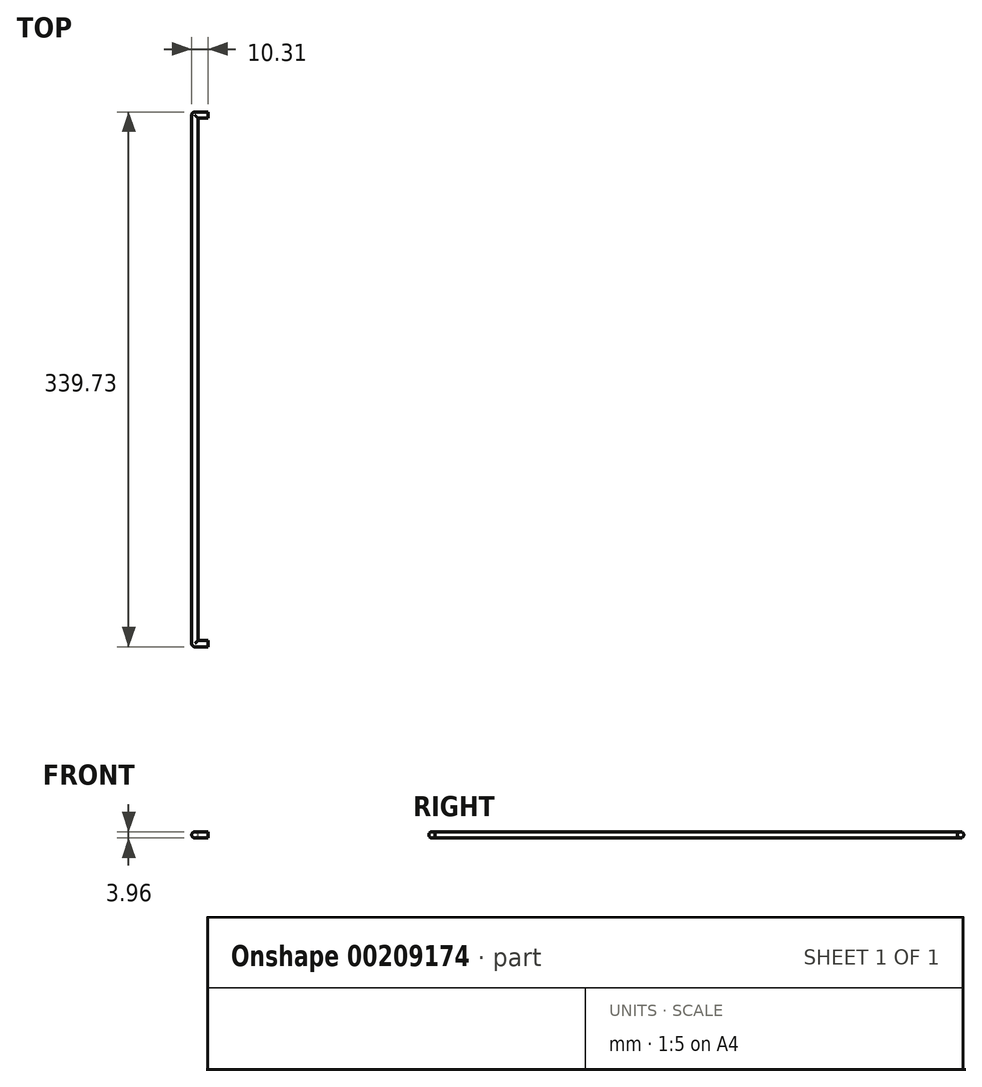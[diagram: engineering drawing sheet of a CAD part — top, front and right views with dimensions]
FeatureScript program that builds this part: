
annotation { "Feature Type Name" : "Feature", "Feature Type Description" : "" }
export const myFeature = defineFeature(function(context is Context, id is Id, definition is map)
    precondition{}
    {
        {
            var Q0;
            Q0=qCreatedBy(makeId("Front.planeOp"),FACE);
            var sketch = newSketch(context, id + "F0", { "sketchPlane" : qUnion([Q0])});
            skLineSegment(sketch, "E0.bottom", {"start": v(1.98, -1.98) * mm, "end": v(-1.98, -1.98) * mm});
            skLineSegment(sketch, "E0.top", {"start": v(1.98, 1.98) * mm, "end": v(-1.98, 1.98) * mm});
            skLineSegment(sketch, "E0.left", {"start": v(1.98, -1.98) * mm, "end": v(1.98, 1.98) * mm});
            skLineSegment(sketch, "E0.right", {"start": v(-1.98, -1.98) * mm, "end": v(-1.98, 1.98) * mm});
            skPoint(sketch, "E0.middle", {"position": v(0, 0) * mm});
            skSolve(sketch);
        }
        {
            var Q0;
            Q0 = qSketchRegion(id + "F0", true);
            extrude(context, id + "F1", {"entities" : qUnion([Q0]), "depth" : 339.72 * mm});
        }
        {
            var Q0;
            Q0=makeQuery(id+"F1.opExtrude","SWEPT_FACE",FACE,{"disambiguationData":[OSD([sQuery(id+"F0.wireOp",EDGE,"E0.left")])]});
            var sketch = newSketch(context, id + "F2", { "sketchPlane" : qUnion([Q0])});
            skLineSegment(sketch, "E1.bottom", {"start": v(-335.76, 1.98) * mm, "end": v(-339.73, 1.98) * mm});
            skLineSegment(sketch, "E1.top", {"start": v(-335.76, -1.98) * mm, "end": v(-339.73, -1.98) * mm});
            skLineSegment(sketch, "E1.left", {"start": v(-335.76, 1.98) * mm, "end": v(-335.76, -1.98) * mm});
            skLineSegment(sketch, "E1.right", {"start": v(-339.73, 1.98) * mm, "end": v(-339.73, -1.98) * mm});
            skPoint(sketch, "E1.middle", {"position": v(-337.74, 0) * mm});
            skLineSegment(sketch, "E2.left", {"start": v(-339.73, 0) * mm, "end": v(-339.73, 0) * mm});
            skLineSegment(sketch, "E2.right", {"start": v(-335.76, 0) * mm, "end": v(-335.76, 0) * mm});
            skLineSegment(sketch, "E3.bottom", {"start": v(0, 1.98) * mm, "end": v(-3.96, 1.98) * mm});
            skLineSegment(sketch, "E3.top", {"start": v(0, -1.98) * mm, "end": v(-3.96, -1.98) * mm});
            skLineSegment(sketch, "E3.left", {"start": v(0, 1.98) * mm, "end": v(0, -1.98) * mm});
            skLineSegment(sketch, "E3.right", {"start": v(-3.96, 1.98) * mm, "end": v(-3.96, -1.98) * mm});
            skPoint(sketch, "E3.middle", {"position": v(-1.98, 0) * mm});
            skSolve(sketch);
        }
        {
            var Q0;
            Q0 = qSketchRegion(id + "F2", true);
            extrude(context, id + "F3", {"entities" : qUnion([Q0]), "operationType" : NewBodyOperationType.ADD, "depth" : 6.35 * mm});
        }
        {
            var Q0;
            Q0=makeQuery(id+"F3.boolean.opBoolean","MERGE",EDGE,{"derivedFrom":[makeQuery(id+"F1.opExtrude","CAP_EDGE",EDGE,{"disambiguationData":[OSD([sQuery(id+"F0.wireOp",EDGE,"E0.top")])],"isStart":true}),makeQuery(id+"F3.opExtrude","SWEPT_EDGE",EDGE,{"disambiguationData":[OSD([sQuery(id+"F2.wireOp",EDGE,"E3.bottom"),sQuery(id+"F2.wireOp",EDGE,"E3.left")])]})]});
            var Q1;
            Q1=makeQuery(id+"F3.opExtrude","SWEPT_EDGE",EDGE,{"disambiguationData":[OSD([sQuery(id+"F0.wireOp",EDGE,"E0.top"),sQuery(id+"F0.wireOp",EDGE,"E0.left"),sQuery(id+"F2.wireOp",EDGE,"E3.bottom"),sQuery(id+"F2.wireOp",EDGE,"E3.right")])]});
            var Q2;
            Q2=makeQuery(id+"F3.boolean.opBoolean","MERGE",EDGE,{"derivedFrom":[makeQuery(id+"F1.opExtrude","CAP_EDGE",EDGE,{"disambiguationData":[OSD([sQuery(id+"F0.wireOp",EDGE,"E0.bottom")])],"isStart":true}),makeQuery(id+"F3.opExtrude","SWEPT_EDGE",EDGE,{"disambiguationData":[OSD([sQuery(id+"F2.wireOp",EDGE,"E3.top"),sQuery(id+"F2.wireOp",EDGE,"E3.left")])]})]});
            var Q3;
            Q3=makeQuery(id+"F3.opExtrude","SWEPT_EDGE",EDGE,{"disambiguationData":[OSD([sQuery(id+"F0.wireOp",EDGE,"E0.bottom"),sQuery(id+"F0.wireOp",EDGE,"E0.left"),sQuery(id+"F2.wireOp",EDGE,"E3.top"),sQuery(id+"F2.wireOp",EDGE,"E3.right")])]});
            var Q4;
            Q4=makeQuery(id+"F1.opExtrude","SWEPT_EDGE",EDGE,{"disambiguationData":[OSD([sQuery(id+"F0.wireOp",EDGE,"E0.top"),sQuery(id+"F0.wireOp",EDGE,"E0.right")])]});
            var Q5;
            Q5=makeQuery(id+"F1.opExtrude","SWEPT_EDGE",EDGE,{"disambiguationData":[OSD([sQuery(id+"F0.wireOp",EDGE,"E0.top"),sQuery(id+"F0.wireOp",EDGE,"E0.left")])]});
            var Q6;
            Q6=makeQuery(id+"F1.opExtrude","SWEPT_EDGE",EDGE,{"disambiguationData":[OSD([sQuery(id+"F0.wireOp",EDGE,"E0.bottom"),sQuery(id+"F0.wireOp",EDGE,"E0.right")])]});
            var Q7;
            Q7=makeQuery(id+"F1.opExtrude","SWEPT_EDGE",EDGE,{"disambiguationData":[OSD([sQuery(id+"F0.wireOp",EDGE,"E0.bottom"),sQuery(id+"F0.wireOp",EDGE,"E0.left")])]});
            var Q8;
            Q8=makeQuery(id+"F1.opExtrude","CAP_EDGE",EDGE,{"disambiguationData":[OSD([sQuery(id+"F0.wireOp",EDGE,"E0.right")])],"isStart":true});
            var Q9;
            Q9=makeQuery(id+"F3.boolean.opBoolean","MERGE",EDGE,{"derivedFrom":[makeQuery(id+"F1.opExtrude","CAP_EDGE",EDGE,{"disambiguationData":[OSD([sQuery(id+"F0.wireOp",EDGE,"E0.top")])],"isStart":false}),makeQuery(id+"F3.opExtrude","SWEPT_EDGE",EDGE,{"disambiguationData":[OSD([sQuery(id+"F2.wireOp",EDGE,"E1.bottom"),sQuery(id+"F2.wireOp",EDGE,"E1.right")])]})]});
            var Q10;
            Q10=makeQuery(id+"F3.opExtrude","SWEPT_EDGE",EDGE,{"disambiguationData":[OSD([sQuery(id+"F0.wireOp",EDGE,"E0.top"),sQuery(id+"F0.wireOp",EDGE,"E0.left"),sQuery(id+"F2.wireOp",EDGE,"E1.bottom"),sQuery(id+"F2.wireOp",EDGE,"E1.left")])]});
            var Q11;
            Q11=makeQuery(id+"F3.opExtrude","SWEPT_EDGE",EDGE,{"disambiguationData":[OSD([sQuery(id+"F0.wireOp",EDGE,"E0.bottom"),sQuery(id+"F0.wireOp",EDGE,"E0.left"),sQuery(id+"F2.wireOp",EDGE,"E1.top"),sQuery(id+"F2.wireOp",EDGE,"E1.left")])]});
            var Q12;
            Q12=makeQuery(id+"F3.boolean.opBoolean","MERGE",EDGE,{"derivedFrom":[makeQuery(id+"F1.opExtrude","CAP_EDGE",EDGE,{"disambiguationData":[OSD([sQuery(id+"F0.wireOp",EDGE,"E0.bottom")])],"isStart":false}),makeQuery(id+"F3.opExtrude","SWEPT_EDGE",EDGE,{"disambiguationData":[OSD([sQuery(id+"F2.wireOp",EDGE,"E1.top"),sQuery(id+"F2.wireOp",EDGE,"E1.right")])]})]});
            var Q13;
            Q13=makeQuery(id+"F1.opExtrude","CAP_EDGE",EDGE,{"disambiguationData":[OSD([sQuery(id+"F0.wireOp",EDGE,"E0.right")])],"isStart":false});
            fillet(context, id + "F4", {"entities" : qUnion([Q0, Q1, Q2, Q3, Q4, Q5, Q6, Q7, Q8, Q9, Q10, Q11, Q12, Q13]), "radius" : 1.98 * mm, "tangentPropagation" : true, "allowEdgeOverflow" : false});
        }
    });
